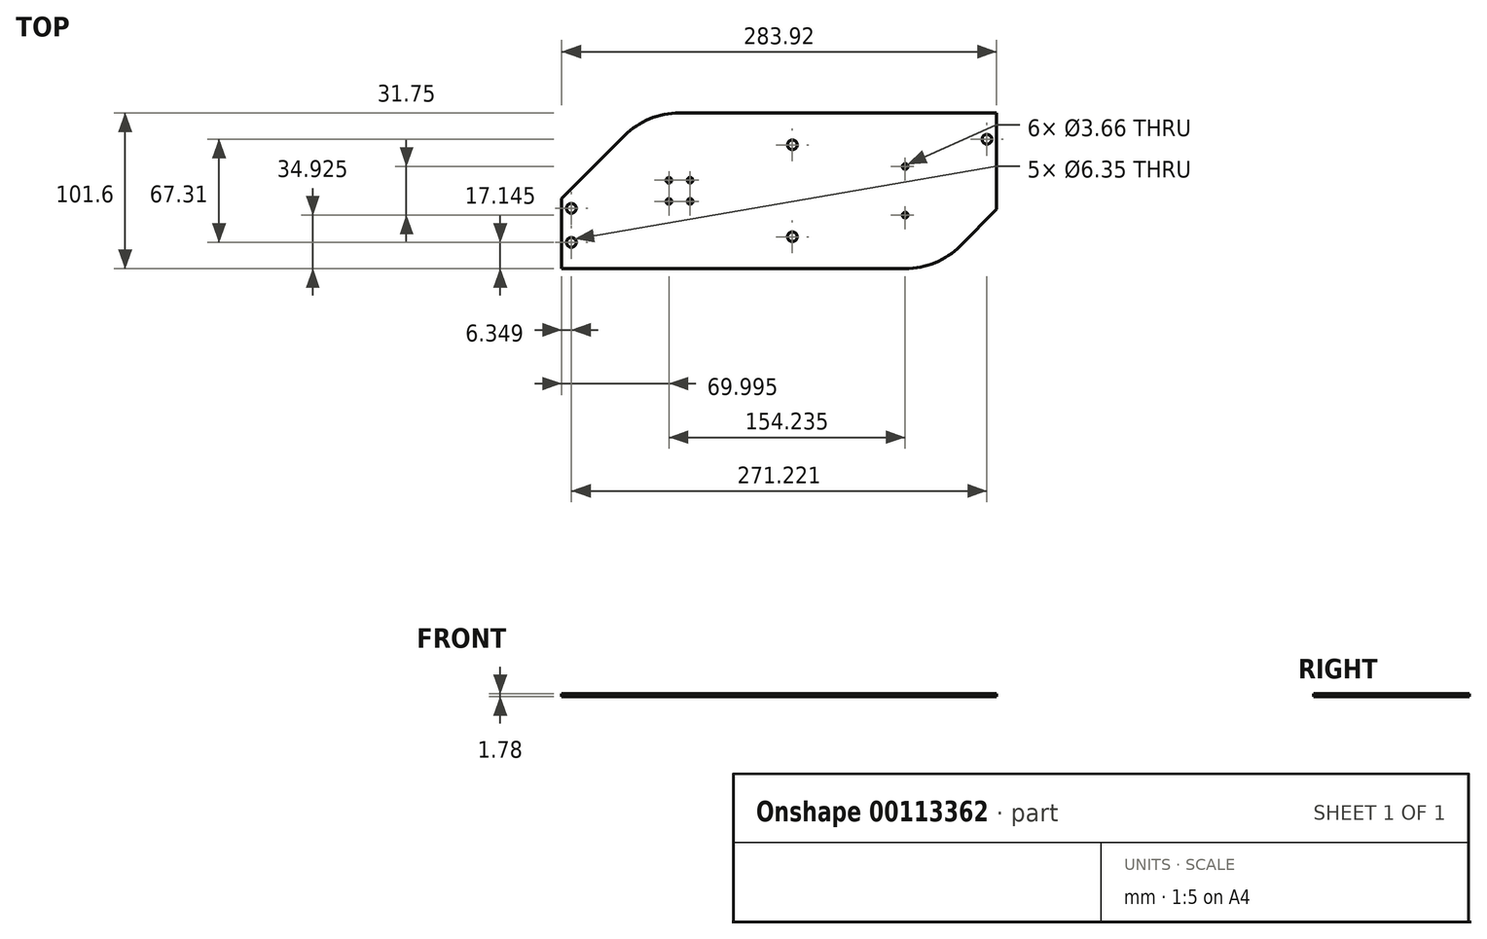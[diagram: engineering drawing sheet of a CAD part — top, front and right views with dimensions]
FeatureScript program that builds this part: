
annotation { "Feature Type Name" : "Feature", "Feature Type Description" : "" }
export const myFeature = defineFeature(function(context is Context, id is Id, definition is map)
    precondition{}
    {
        {
            var Q0;
            Q0=qCreatedBy(makeId("Top.planeOp"),FACE);
            var sketch = newSketch(context, id + "F0", { "sketchPlane" : qUnion([Q0])});
            skLineSegment(sketch, "E0.bottom", {"start": v(133.35, 50.8) * mm, "end": v(-133.35, 50.8) * mm});
            skLineSegment(sketch, "E0.top", {"start": v(133.35, -50.8) * mm, "end": v(-133.35, -50.8) * mm});
            skLineSegment(sketch, "E0.left", {"start": v(133.35, 50.8) * mm, "end": v(133.35, -50.8) * mm});
            skLineSegment(sketch, "E0.right", {"start": v(-133.35, 50.8) * mm, "end": v(-133.35, -50.8) * mm});
            skPoint(sketch, "E0.middle", {"position": v(0, 0) * mm});
            skCircle(sketch, "E1", {"center": v(73.66, 0) * mm, "radius": 9.78 * mm, "construction": true});
            skCircle(sketch, "E2", {"center": v(-73.66, 0) * mm, "radius": 25.4 * mm, "construction": true});
            skCircle(sketch, "E3", {"center": v(-73.66, 0) * mm, "radius": 50.8 * mm});
            skCircle(sketch, "E4", {"center": v(-73.66, 0) * mm, "radius": 53.98 * mm, "construction": true});
            skCircle(sketch, "E5", {"center": v(73.66, 0) * mm, "radius": 53.98 * mm, "construction": true});
            skCircle(sketch, "E6", {"center": v(73.66, 0) * mm, "radius": 50.8 * mm});
            skCircle(sketch, "E7", {"center": v(-254, 41.73) * mm, "radius": 12.7 * mm, "construction": true});
            skCircle(sketch, "E8", {"center": v(0, 29.97) * mm, "radius": 15.24 * mm, "construction": true});
            skCircle(sketch, "E9", {"center": v(-254, -40.97) * mm, "radius": 12.7 * mm, "construction": true});
            skCircle(sketch, "E10", {"center": v(0, -29.97) * mm, "radius": 15.24 * mm, "construction": true});
            skCircle(sketch, "E11", {"center": v(-73.66, 0) * mm, "radius": 45.21 * mm, "construction": true});
            skCircle(sketch, "E12", {"center": v(73.66, 0) * mm, "radius": 45.21 * mm, "construction": true});
            skLineSegment(sketch, "E13", {"start": v(-73.66, 45.21) * mm, "end": v(73.66, 45.21) * mm, "construction": true});
            skLineSegment(sketch, "E14", {"start": v(-73.66, -45.21) * mm, "end": v(73.66, -45.21) * mm, "construction": true});
            skCircle(sketch, "E15", {"center": v(0, 29.97) * mm, "radius": 3.18 * mm});
            skCircle(sketch, "E16", {"center": v(0, -29.97) * mm, "radius": 3.18 * mm});
            skLineSegment(sketch, "E17", {"start": v(73.66, 0) * mm, "end": v(73.66, 9.78) * mm, "construction": true});
            skLineSegment(sketch, "E18", {"start": v(66.75, 6.91) * mm, "end": v(80.57, -6.91) * mm, "construction": true});
            skLineSegment(sketch, "E19", {"start": v(66.75, -6.91) * mm, "end": v(80.57, 6.91) * mm, "construction": true});
            skCircle(sketch, "E20", {"center": v(66.75, 6.91) * mm, "radius": 1.83 * mm});
            skCircle(sketch, "E21", {"center": v(80.57, 6.91) * mm, "radius": 1.83 * mm});
            skCircle(sketch, "E22", {"center": v(66.75, -6.91) * mm, "radius": 1.83 * mm});
            skCircle(sketch, "E23", {"center": v(80.57, -6.91) * mm, "radius": 1.83 * mm});
            skLineSegment(sketch, "E24", {"start": v(-133.35, 12.15) * mm, "end": v(-109.58, 35.92) * mm});
            skLineSegment(sketch, "E25", {"start": v(109.58, -35.92) * mm, "end": v(133.35, -12.15) * mm});
            skCircle(sketch, "E26", {"center": v(-144.22, -33.66) * mm, "radius": 3.18 * mm});
            skCircle(sketch, "E27", {"center": v(127, 33.66) * mm, "radius": 3.18 * mm});
            skCircle(sketch, "E28", {"center": v(-144.22, -33.66) * mm, "radius": 6.99 * mm, "construction": true});
            skCircle(sketch, "E29", {"center": v(127, 33.66) * mm, "radius": 6.99 * mm, "construction": true});
            skLineSegment(sketch, "E30", {"start": v(-109.58, 35.92) * mm, "end": v(-196.3, -50.8) * mm, "construction": true});
            skLineSegment(sketch, "E31", {"start": v(-196.3, -50.8) * mm, "end": v(-133.35, -50.8) * mm, "construction": true});
            skLineSegment(sketch, "E32", {"start": v(109.58, -35.92) * mm, "end": v(196.3, 50.8) * mm, "construction": true});
            skLineSegment(sketch, "E33", {"start": v(196.3, 50.8) * mm, "end": v(133.35, 50.8) * mm, "construction": true});
            skCircle(sketch, "E34", {"center": v(-73.66, 15.88) * mm, "radius": 1.83 * mm});
            skCircle(sketch, "E35", {"center": v(-73.66, -15.88) * mm, "radius": 1.83 * mm});
            skLineSegment(sketch, "E36", {"start": v(-150.57, -50.8) * mm, "end": v(-150.57, -5.07) * mm});
            skLineSegment(sketch, "E37", {"start": v(-150.57, -5.07) * mm, "end": v(-133.35, 12.15) * mm});
            skLineSegment(sketch, "E38", {"start": v(-133.35, -50.8) * mm, "end": v(-150.57, -50.8) * mm});
            skCircle(sketch, "E39", {"center": v(-144.22, -11.43) * mm, "radius": 3.18 * mm});
            skCircle(sketch, "E40", {"center": v(-144.22, -11.43) * mm, "radius": 6.99 * mm, "construction": true});
            skPoint(sketch, "E41", {"position": v(-128.7, 16.8) * mm});
            skCircle(sketch, "E42", {"center": v(73.66, 15.88) * mm, "radius": 1.83 * mm});
            skCircle(sketch, "E43", {"center": v(73.66, -15.88) * mm, "radius": 1.83 * mm});
            skCircle(sketch, "E44", {"center": v(-73.66, 0) * mm, "radius": 9.78 * mm, "construction": true});
            skCircle(sketch, "E45", {"center": v(-80.57, 6.91) * mm, "radius": 1.83 * mm});
            skCircle(sketch, "E46", {"center": v(-66.75, 6.91) * mm, "radius": 1.83 * mm});
            skCircle(sketch, "E47", {"center": v(-80.57, -6.91) * mm, "radius": 1.83 * mm});
            skCircle(sketch, "E48", {"center": v(-66.75, -6.91) * mm, "radius": 1.83 * mm});
            skLineSegment(sketch, "E49", {"start": v(-73.66, 0) * mm, "end": v(-73.66, 9.78) * mm, "construction": true});
            skLineSegment(sketch, "E50", {"start": v(-73.66, 0) * mm, "end": v(-66.75, 6.91) * mm, "construction": true});
            skLineSegment(sketch, "E51", {"start": v(-73.66, 0) * mm, "end": v(-80.57, 6.91) * mm, "construction": true});
            skLineSegment(sketch, "E52", {"start": v(-73.66, 0) * mm, "end": v(-80.57, -6.91) * mm, "construction": true});
            skLineSegment(sketch, "E53", {"start": v(-73.66, 0) * mm, "end": v(-66.75, -6.91) * mm, "construction": true});
            skSolve(sketch);
        }
        {
            var Q0;
            {var subQ4=sQuery(id+"F0.wireOp",EDGE,"E25");Q0=makeQuery(id+"F0.imprint","IMPRINT",FACE,{"disambiguationData":[TD([[makeQuery(id+"F0.imprint","IMPRINT",EDGE,{"derivedFrom":subQ4}),1.0]])]});}
            var Q1;
            Q1=makeQuery(id+"F0.imprint","IMPRINT",FACE,{"disambiguationData":[TD([[makeQuery(id+"F0.imprint","IMPRINT",EDGE,{"derivedFrom":sQuery(id+"F0.wireOp",EDGE,"E20")}),-1.0]])]});
            var Q2;
            Q2=makeQuery(id+"F0.imprint","IMPRINT",FACE,{"disambiguationData":[TD([[makeQuery(id+"F0.imprint","IMPRINT",EDGE,{"derivedFrom":sQuery(id+"F0.wireOp",EDGE,"E15")}),-1.0]])]});
            var Q3;
            {var subQ5=sQuery(id+"F0.wireOp",EDGE,"E24");Q3=makeQuery(id+"F0.imprint","IMPRINT",FACE,{"disambiguationData":[TD([[makeQuery(id+"F0.imprint","IMPRINT",EDGE,{"derivedFrom":subQ5}),-1.0]])]});}
            var Q4;
            Q4=makeQuery(id+"F0.imprint","IMPRINT",FACE,{"disambiguationData":[TD([[makeQuery(id+"F0.imprint","IMPRINT",EDGE,{"derivedFrom":sQuery(id+"F0.wireOp",EDGE,"E26")}),-1.0]])]});
            var Q5;
            Q5=makeQuery(id+"F0.imprint","IMPRINT",FACE,{"disambiguationData":[TD([[makeQuery(id+"F0.imprint","IMPRINT",EDGE,{"derivedFrom":sQuery(id+"F0.wireOp",EDGE,"E34")}),-1.0]])]});
            var Q6;
            Q6=makeQuery(id+"F0.imprint","IMPRINT",FACE,{"disambiguationData":[TD([[makeQuery(id+"F0.imprint","IMPRINT",EDGE,{"derivedFrom":sQuery(id+"F0.wireOp",EDGE,"E34")}),1.0]])]});
            var Q7;
            Q7=makeQuery(id+"F0.imprint","IMPRINT",FACE,{"disambiguationData":[TD([[makeQuery(id+"F0.imprint","IMPRINT",EDGE,{"derivedFrom":sQuery(id+"F0.wireOp",EDGE,"E35")}),1.0]])]});
            var Q8;
            Q8=makeQuery(id+"F0.imprint","IMPRINT",FACE,{"disambiguationData":[TD([[makeQuery(id+"F0.imprint","IMPRINT",EDGE,{"derivedFrom":sQuery(id+"F0.wireOp",EDGE,"E20")}),1.0]])]});
            var Q9;
            Q9=makeQuery(id+"F0.imprint","IMPRINT",FACE,{"disambiguationData":[TD([[makeQuery(id+"F0.imprint","IMPRINT",EDGE,{"derivedFrom":sQuery(id+"F0.wireOp",EDGE,"E22")}),1.0]])]});
            var Q10;
            Q10=makeQuery(id+"F0.imprint","IMPRINT",FACE,{"disambiguationData":[TD([[makeQuery(id+"F0.imprint","IMPRINT",EDGE,{"derivedFrom":sQuery(id+"F0.wireOp",EDGE,"E21")}),1.0]])]});
            var Q11;
            Q11=makeQuery(id+"F0.imprint","IMPRINT",FACE,{"disambiguationData":[TD([[makeQuery(id+"F0.imprint","IMPRINT",EDGE,{"derivedFrom":sQuery(id+"F0.wireOp",EDGE,"E23")}),1.0]])]});
            extrude(context, id + "F1", {"entities" : qUnion([Q0, Q1, Q2, Q3, Q4, Q5, Q6, Q7, Q8, Q9, Q10, Q11]), "depth" : 1.78 * mm, "offsetDistance" : 25.4 * mm});
        }
    });
